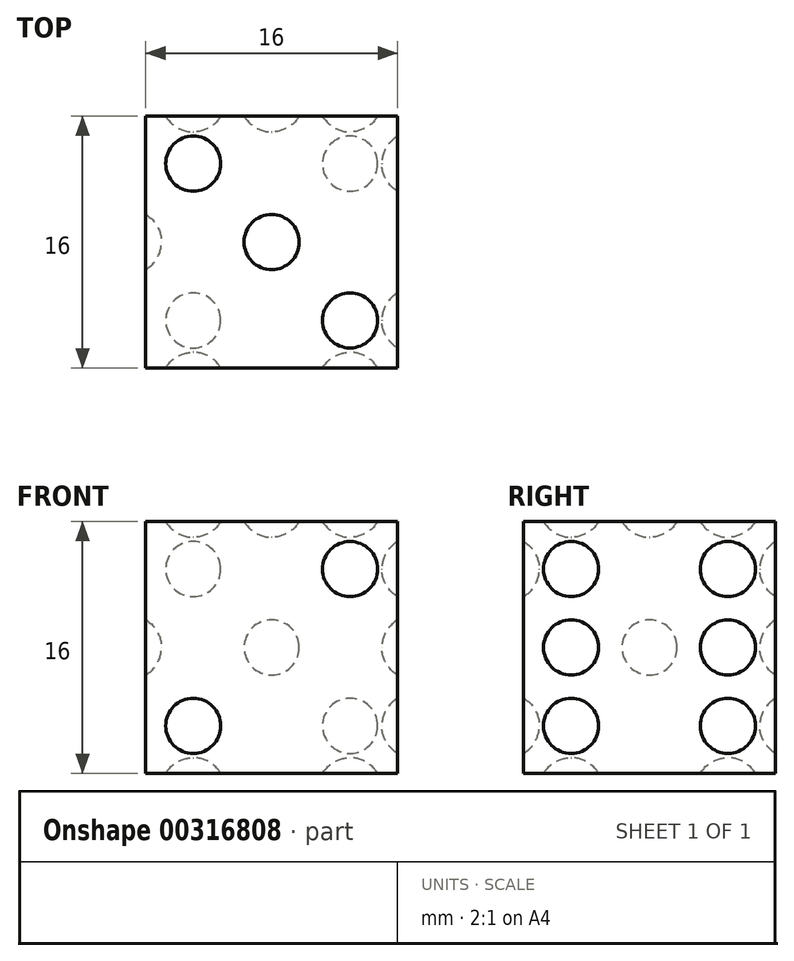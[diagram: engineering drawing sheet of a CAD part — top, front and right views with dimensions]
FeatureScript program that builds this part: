
annotation { "Feature Type Name" : "Feature", "Feature Type Description" : "" }
export const myFeature = defineFeature(function(context is Context, id is Id, definition is map)
    precondition{}
    {
        {
            var Q0;
            Q0=qCreatedBy(makeId("Top.planeOp"),FACE);
            var sketch = newSketch(context, id + "F0", { "sketchPlane" : qUnion([Q0])});
            skLineSegment(sketch, "E0.bottom", {"start": v(8, 8) * mm, "end": v(-8, 8) * mm});
            skLineSegment(sketch, "E0.top", {"start": v(8, -8) * mm, "end": v(-8, -8) * mm});
            skLineSegment(sketch, "E0.left", {"start": v(8, 8) * mm, "end": v(8, -8) * mm});
            skLineSegment(sketch, "E0.right", {"start": v(-8, 8) * mm, "end": v(-8, -8) * mm});
            skPoint(sketch, "E0.middle", {"position": v(0, 0) * mm});
            skSolve(sketch);
        }
        {
            var Q0;
            Q0 = qSketchRegion(id + "F0", true);
            extrude(context, id + "F1", {"entities" : qUnion([Q0]), "endBound" : BoundingType.SYMMETRIC, "depth" : 16 * mm});
        }
        {
            var Q0;
            Q0=makeQuery(id+"F1.opExtrude","CAP_FACE",FACE,{"disambiguationData":[OSD([sQuery(id+"F0.wireOp",EDGE,"E0.bottom"),sQuery(id+"F0.wireOp",EDGE,"E0.top"),sQuery(id+"F0.wireOp",EDGE,"E0.left"),sQuery(id+"F0.wireOp",EDGE,"E0.right")])],"isStart":false});
            var sketch = newSketch(context, id + "F2", { "sketchPlane" : qUnion([Q0])});
            skCircle(sketch, "E1", {"center": v(0, 0) * mm, "radius": 1.75 * mm});
            skCircle(sketch, "E2", {"center": v(-4.98, 4.98) * mm, "radius": 1.75 * mm});
            skCircle(sketch, "E3", {"center": v(4.98, -4.98) * mm, "radius": 1.75 * mm});
            skSolve(sketch);
        }
        {
            var Q0;
            Q0 = qSketchRegion(id + "F2", true);
            extrude(context, id + "F3", {"entities" : qUnion([Q0]), "operationType" : NewBodyOperationType.REMOVE, "oppositeDirection" : true, "depth" : 1 * mm});
        }
        {
            var Q0;
            Q0=makeQuery(id+"F1.opExtrude","SWEPT_FACE",FACE,{"disambiguationData":[OSD([sQuery(id+"F0.wireOp",EDGE,"E0.top")])]});
            var sketch = newSketch(context, id + "F4", { "sketchPlane" : qUnion([Q0])});
            skCircle(sketch, "E4", {"center": v(4.98, 4.98) * mm, "radius": 1.75 * mm});
            skCircle(sketch, "E5", {"center": v(-4.98, -4.98) * mm, "radius": 1.75 * mm});
            skSolve(sketch);
        }
        {
            var Q0;
            Q0 = qSketchRegion(id + "F4", true);
            extrude(context, id + "F5", {"entities" : qUnion([Q0]), "operationType" : NewBodyOperationType.REMOVE, "oppositeDirection" : true, "depth" : 1 * mm});
        }
        {
            var Q0;
            Q0=makeQuery(id+"F1.opExtrude","SWEPT_FACE",FACE,{"disambiguationData":[OSD([sQuery(id+"F0.wireOp",EDGE,"E0.right")])]});
            var sketch = newSketch(context, id + "F6", { "sketchPlane" : qUnion([Q0])});
            skCircle(sketch, "E6", {"center": v(0, 0) * mm, "radius": 1.75 * mm});
            skSolve(sketch);
        }
        {
            var Q0;
            Q0 = qSketchRegion(id + "F6", true);
            extrude(context, id + "F7", {"entities" : qUnion([Q0]), "operationType" : NewBodyOperationType.REMOVE, "oppositeDirection" : true, "depth" : 1 * mm});
        }
        {
            var Q0;
            Q0=makeQuery(id+"F1.opExtrude","SWEPT_FACE",FACE,{"disambiguationData":[OSD([sQuery(id+"F0.wireOp",EDGE,"E0.bottom")])]});
            var sketch = newSketch(context, id + "F8", { "sketchPlane" : qUnion([Q0])});
            skCircle(sketch, "E7", {"center": v(0, 0) * mm, "radius": 1.75 * mm});
            skCircle(sketch, "E8", {"center": v(-4.98, 4.98) * mm, "radius": 1.75 * mm});
            skCircle(sketch, "E9", {"center": v(4.98, 4.98) * mm, "radius": 1.75 * mm});
            skCircle(sketch, "E10", {"center": v(4.98, -4.98) * mm, "radius": 1.75 * mm});
            skCircle(sketch, "E11", {"center": v(-4.98, -4.98) * mm, "radius": 1.75 * mm});
            skSolve(sketch);
        }
        {
            var Q0;
            Q0 = qSketchRegion(id + "F8", true);
            extrude(context, id + "F9", {"entities" : qUnion([Q0]), "operationType" : NewBodyOperationType.REMOVE, "oppositeDirection" : true, "depth" : 1 * mm});
        }
        {
            var Q0;
            Q0=makeQuery(id+"F1.opExtrude","CAP_FACE",FACE,{"disambiguationData":[OSD([sQuery(id+"F0.wireOp",EDGE,"E0.bottom"),sQuery(id+"F0.wireOp",EDGE,"E0.top"),sQuery(id+"F0.wireOp",EDGE,"E0.left"),sQuery(id+"F0.wireOp",EDGE,"E0.right")])],"isStart":true});
            var sketch = newSketch(context, id + "F10", { "sketchPlane" : qUnion([Q0])});
            skCircle(sketch, "E12", {"center": v(-4.98, 4.98) * mm, "radius": 1.75 * mm});
            skCircle(sketch, "E13", {"center": v(4.98, 4.98) * mm, "radius": 1.75 * mm});
            skCircle(sketch, "E14", {"center": v(4.98, -4.98) * mm, "radius": 1.75 * mm});
            skCircle(sketch, "E15", {"center": v(-4.98, -4.98) * mm, "radius": 1.75 * mm});
            skSolve(sketch);
        }
        {
            var Q0;
            Q0 = qSketchRegion(id + "F10", true);
            extrude(context, id + "F11", {"entities" : qUnion([Q0]), "operationType" : NewBodyOperationType.REMOVE, "oppositeDirection" : true, "depth" : 1 * mm});
        }
        {
            var Q0;
            Q0=makeQuery(id+"F1.opExtrude","SWEPT_FACE",FACE,{"disambiguationData":[OSD([sQuery(id+"F0.wireOp",EDGE,"E0.left")])]});
            var sketch = newSketch(context, id + "F12", { "sketchPlane" : qUnion([Q0])});
            skCircle(sketch, "E16", {"center": v(-4.98, 4.98) * mm, "radius": 1.75 * mm});
            skCircle(sketch, "E17", {"center": v(-4.98, 0) * mm, "radius": 1.75 * mm});
            skCircle(sketch, "E18", {"center": v(-4.98, -4.98) * mm, "radius": 1.75 * mm});
            skCircle(sketch, "E19", {"center": v(4.98, -4.98) * mm, "radius": 1.75 * mm});
            skCircle(sketch, "E20", {"center": v(4.98, 0) * mm, "radius": 1.75 * mm});
            skCircle(sketch, "E21", {"center": v(4.98, 4.98) * mm, "radius": 1.75 * mm});
            skSolve(sketch);
        }
        {
            var Q0;
            Q0 = qSketchRegion(id + "F12", true);
            extrude(context, id + "F13", {"entities" : qUnion([Q0]), "operationType" : NewBodyOperationType.REMOVE, "oppositeDirection" : true, "depth" : 1 * mm});
        }
        {
            var Q0;
            Q0=makeQuery(id+"F3.boolean.opBoolean","COPY",FACE,{"derivedFrom":makeQuery(id+"F3.opExtrude","CAP_FACE",FACE,{"disambiguationData":[OSD([sQuery(id+"F2.wireOp",EDGE,"E3")])],"isStart":false})});
            var Q1;
            Q1=makeQuery(id+"F3.boolean.opBoolean","COPY",FACE,{"derivedFrom":makeQuery(id+"F3.opExtrude","CAP_FACE",FACE,{"disambiguationData":[OSD([sQuery(id+"F2.wireOp",EDGE,"E1")])],"isStart":false})});
            var Q2;
            Q2=makeQuery(id+"F3.boolean.opBoolean","COPY",FACE,{"derivedFrom":makeQuery(id+"F3.opExtrude","CAP_FACE",FACE,{"disambiguationData":[OSD([sQuery(id+"F2.wireOp",EDGE,"E2")])],"isStart":false})});
            var Q3;
            Q3=makeQuery(id+"F5.boolean.opBoolean","COPY",FACE,{"derivedFrom":makeQuery(id+"F5.opExtrude","CAP_FACE",FACE,{"disambiguationData":[OSD([sQuery(id+"F4.wireOp",EDGE,"E4")])],"isStart":false})});
            var Q4;
            Q4=makeQuery(id+"F5.boolean.opBoolean","COPY",FACE,{"derivedFrom":makeQuery(id+"F5.opExtrude","CAP_FACE",FACE,{"disambiguationData":[OSD([sQuery(id+"F4.wireOp",EDGE,"E5")])],"isStart":false})});
            var Q5;
            Q5=makeQuery(id+"F7.boolean.opBoolean","COPY",FACE,{"derivedFrom":makeQuery(id+"F7.opExtrude","CAP_FACE",FACE,{"disambiguationData":[OSD([sQuery(id+"F6.wireOp",EDGE,"E6")])],"isStart":false})});
            var Q6;
            Q6=makeQuery(id+"F9.boolean.opBoolean","COPY",FACE,{"derivedFrom":makeQuery(id+"F9.opExtrude","CAP_FACE",FACE,{"disambiguationData":[OSD([sQuery(id+"F8.wireOp",EDGE,"E8")])],"isStart":false})});
            var Q7;
            Q7=makeQuery(id+"F9.boolean.opBoolean","COPY",FACE,{"derivedFrom":makeQuery(id+"F9.opExtrude","CAP_FACE",FACE,{"disambiguationData":[OSD([sQuery(id+"F8.wireOp",EDGE,"E7")])],"isStart":false})});
            var Q8;
            Q8=makeQuery(id+"F9.boolean.opBoolean","COPY",FACE,{"derivedFrom":makeQuery(id+"F9.opExtrude","CAP_FACE",FACE,{"disambiguationData":[OSD([sQuery(id+"F8.wireOp",EDGE,"E9")])],"isStart":false})});
            var Q9;
            Q9=makeQuery(id+"F9.boolean.opBoolean","COPY",FACE,{"derivedFrom":makeQuery(id+"F9.opExtrude","CAP_FACE",FACE,{"disambiguationData":[OSD([sQuery(id+"F8.wireOp",EDGE,"E10")])],"isStart":false})});
            var Q10;
            Q10=makeQuery(id+"F9.boolean.opBoolean","COPY",FACE,{"derivedFrom":makeQuery(id+"F9.opExtrude","CAP_FACE",FACE,{"disambiguationData":[OSD([sQuery(id+"F8.wireOp",EDGE,"E11")])],"isStart":false})});
            var Q11;
            Q11=makeQuery(id+"F11.boolean.opBoolean","COPY",FACE,{"derivedFrom":makeQuery(id+"F11.opExtrude","CAP_FACE",FACE,{"disambiguationData":[OSD([sQuery(id+"F10.wireOp",EDGE,"E12")])],"isStart":false})});
            var Q12;
            Q12=makeQuery(id+"F11.boolean.opBoolean","COPY",FACE,{"derivedFrom":makeQuery(id+"F11.opExtrude","CAP_FACE",FACE,{"disambiguationData":[OSD([sQuery(id+"F10.wireOp",EDGE,"E13")])],"isStart":false})});
            var Q13;
            Q13=makeQuery(id+"F11.boolean.opBoolean","COPY",FACE,{"derivedFrom":makeQuery(id+"F11.opExtrude","CAP_FACE",FACE,{"disambiguationData":[OSD([sQuery(id+"F10.wireOp",EDGE,"E14")])],"isStart":false})});
            var Q14;
            Q14=makeQuery(id+"F11.boolean.opBoolean","COPY",FACE,{"derivedFrom":makeQuery(id+"F11.opExtrude","CAP_FACE",FACE,{"disambiguationData":[OSD([sQuery(id+"F10.wireOp",EDGE,"E15")])],"isStart":false})});
            var Q15;
            Q15=makeQuery(id+"F13.boolean.opBoolean","COPY",FACE,{"derivedFrom":makeQuery(id+"F13.opExtrude","CAP_FACE",FACE,{"disambiguationData":[OSD([sQuery(id+"F12.wireOp",EDGE,"E20")])],"isStart":false})});
            var Q16;
            Q16=makeQuery(id+"F13.boolean.opBoolean","COPY",FACE,{"derivedFrom":makeQuery(id+"F13.opExtrude","CAP_FACE",FACE,{"disambiguationData":[OSD([sQuery(id+"F12.wireOp",EDGE,"E19")])],"isStart":false})});
            var Q17;
            Q17=makeQuery(id+"F13.boolean.opBoolean","COPY",FACE,{"derivedFrom":makeQuery(id+"F13.opExtrude","CAP_FACE",FACE,{"disambiguationData":[OSD([sQuery(id+"F12.wireOp",EDGE,"E18")])],"isStart":false})});
            var Q18;
            Q18=makeQuery(id+"F13.boolean.opBoolean","COPY",FACE,{"derivedFrom":makeQuery(id+"F13.opExtrude","CAP_FACE",FACE,{"disambiguationData":[OSD([sQuery(id+"F12.wireOp",EDGE,"E17")])],"isStart":false})});
            var Q19;
            Q19=makeQuery(id+"F13.boolean.opBoolean","COPY",FACE,{"derivedFrom":makeQuery(id+"F13.opExtrude","CAP_FACE",FACE,{"disambiguationData":[OSD([sQuery(id+"F12.wireOp",EDGE,"E16")])],"isStart":false})});
            var Q20;
            Q20=makeQuery(id+"F13.boolean.opBoolean","COPY",FACE,{"derivedFrom":makeQuery(id+"F13.opExtrude","CAP_FACE",FACE,{"disambiguationData":[OSD([sQuery(id+"F12.wireOp",EDGE,"E21")])],"isStart":false})});
            fillet(context, id + "F14", {"entities" : qUnion([Q0, Q1, Q2, Q3, Q4, Q5, Q6, Q7, Q8, Q9, Q10, Q11, Q12, Q13, Q14, Q15, Q16, Q17, Q18, Q19, Q20]), "radius" : 2 * mm, "tangentPropagation" : true, "allowEdgeOverflow" : false});
        }
    });
